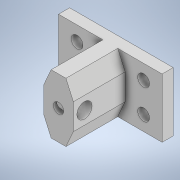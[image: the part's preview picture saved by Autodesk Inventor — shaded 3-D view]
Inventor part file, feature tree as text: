
AUTODESK INVENTOR PART (.ipt)
format: ipt  version: 2021 (Build 250183000, 183)  size: 148,992 bytes
history: native  units: mm
features: extrude x4, sketch x4
ambient origin geometry x8: Origin, YZ Plane, XZ Plane, XY Plane, X Axis, Y Axis, Z Axis, Center Point
bodies: Solid1 (feature_tree)
feature tree (8):
  extrude  "Extrusion1"  Depth=16.0mm
  extrude  "Extrusion2"  Depth=9.0mm
  extrude  "Extrusion3"  Depth=4.0mm
  extrude  "Extrusion4"  Depth=3.0mm TaperAngle=0.0deg
  sketch  "Sketch1"  dims[d0=28.0mm d1=16.0mm]
  sketch  "Sketch2"  dims[d2=18.0mm d3=9.0mm]
  sketch  "Sketch3"  dims[d4=8.0mm d5=4.0mm]
  sketch  "Sketch4"  dims[d6=3.2mm d7=3.0mm d8=0.0mm d9=8.0mm d10=4.0mm d11=7.0mm d12=14.0mm d13=0.0mm d14=3.0mm d15=4.1mm d16=0.0mm d17=0.0mm d18=2.8mm d19=3.0mm d20=0.0mm]
